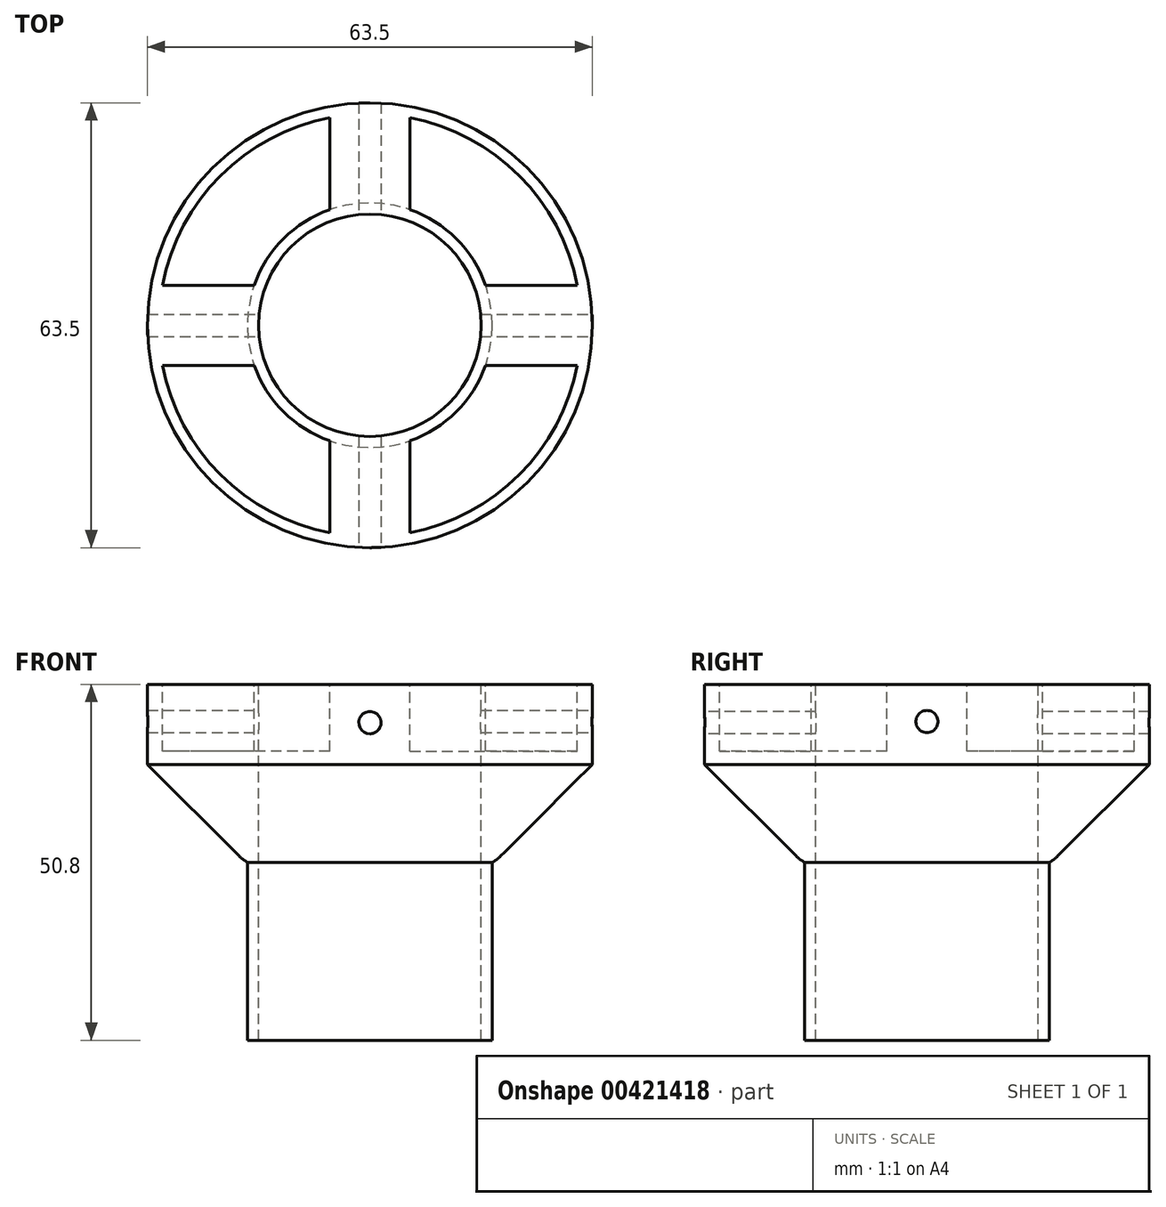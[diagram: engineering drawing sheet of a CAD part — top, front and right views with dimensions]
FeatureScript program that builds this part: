
annotation { "Feature Type Name" : "Feature", "Feature Type Description" : "" }
export const myFeature = defineFeature(function(context is Context, id is Id, definition is map)
    precondition{}
    {
        {
            var Q0;
            Q0=qCreatedBy(makeId("Top.planeOp"),FACE);
            var sketch = newSketch(context, id + "F0", { "sketchPlane" : qUnion([Q0])});
            skCircle(sketch, "E0", {"center": v(0, 0) * mm, "radius": 31.75 * mm});
            skCircle(sketch, "E1", {"center": v(0, 0) * mm, "radius": 15.88 * mm});
            skCircle(sketch, "E2", {"center": v(0, 0) * mm, "radius": 17.46 * mm});
            skSolve(sketch);
        }
        {
            var Q0;
            Q0 = qSketchRegion(id + "F0", true);
            extrude(context, id + "F1", {"entities" : qUnion([Q0]), "oppositeDirection" : true, "depth" : 25.4 * mm});
        }
        {
            var Q0;
            Q0=makeQuery(id+"F0.imprint","IMPRINT",FACE,{"disambiguationData":[TD([[makeQuery(id+"F0.imprint","IMPRINT",EDGE,{"derivedFrom":sQuery(id+"F0.wireOp",EDGE,"E1")}),-1.0]])]});
            extrude(context, id + "F2", {"entities" : qUnion([Q0]), "operationType" : NewBodyOperationType.ADD, "oppositeDirection" : true, "depth" : 50.8 * mm});
        }
        {
            var Q0;
            Q0=makeQuery(id+"F1.opExtrude","CAP_EDGE",EDGE,{"disambiguationData":[OSD([sQuery(id+"F0.wireOp",EDGE,"E0")])],"isStart":false});
            chamfer(context, id + "F3", {"entities" : qUnion([Q0]), "width" : 13.97 * mm, "tangentPropagation" : true});
        }
        {
            var Q0;
            {var subQ0=sQuery(id+"F0.wireOp",EDGE,"E0");Q0=makeQuery(id+"F3.opChamfer","BLEND_EDGE",EDGE,{"blendedFrom":[makeQuery(id+"F1.opExtrude","CAP_EDGE",EDGE,{"disambiguationData":[OSD([subQ0])],"isStart":false}),makeQuery(id+"F1.opExtrude","CAP_FACE",FACE,{"disambiguationData":[OSD([subQ0,sQuery(id+"F0.wireOp",EDGE,"E2")])],"isStart":false})],"blendedInto":[makeQuery(id+"F1.opExtrude","CAP_FACE",FACE,{"disambiguationData":[OSD([subQ0,sQuery(id+"F0.wireOp",EDGE,"E2")])],"isStart":false})]});}
            fillet(context, id + "F4", {"entities" : qUnion([Q0]), "radius" : 5.08 * mm, "tangentPropagation" : true, "allowEdgeOverflow" : false});
        }
        {
            var Q0;
            Q0=qCreatedBy(makeId("Top.planeOp"),FACE);
            var sketch = newSketch(context, id + "F5", { "sketchPlane" : qUnion([Q0])});
            skLineSegment(sketch, "E3.bottom", {"start": v(5.72, -31.75) * mm, "end": v(-5.71, -31.75) * mm});
            skLineSegment(sketch, "E3.top", {"start": v(5.71, 31.75) * mm, "end": v(-5.72, 31.75) * mm});
            skLineSegment(sketch, "E3.left", {"start": v(5.72, -31.75) * mm, "end": v(5.71, 31.75) * mm});
            skLineSegment(sketch, "E3.right", {"start": v(-5.72, -31.75) * mm, "end": v(-5.72, 31.75) * mm});
            skPoint(sketch, "E3.middle", {"position": v(0, 0) * mm});
            skLineSegment(sketch, "E4.bottom", {"start": v(31.75, -5.71) * mm, "end": v(-31.75, -5.72) * mm});
            skLineSegment(sketch, "E4.top", {"start": v(31.75, 5.72) * mm, "end": v(-31.75, 5.71) * mm});
            skLineSegment(sketch, "E4.left", {"start": v(31.75, -5.71) * mm, "end": v(31.75, 5.72) * mm});
            skLineSegment(sketch, "E4.right", {"start": v(-31.75, -5.72) * mm, "end": v(-31.75, 5.71) * mm});
            skCircle(sketch, "E5", {"center": v(0, 0) * mm, "radius": 30.16 * mm});
            skCircle(sketch, "E6", {"center": v(0, 0) * mm, "radius": 17.46 * mm});
            skSolve(sketch);
        }
        {
            var Q0;
            {var subQ0=sQuery(id+"F5.wireOp",EDGE,"E5");var subQ1=sQuery(id+"F5.wireOp",EDGE,"E3.right");var subQ2=makeQuery(id+"F5.imprint","INTERSECT",VERTEX,{"disambiguationData":[OD(1.0)],"derivedFrom":[subQ1,subQ0]});Q0=makeQuery(id+"F5.imprint","IMPRINT",FACE,{"disambiguationData":[TD([[makeQuery(id+"F5.imprint","IMPRINT",EDGE,{"disambiguationData":[TD([[subQ2,1.0]])],"derivedFrom":subQ1}),1.0]])]});}
            var Q1;
            {var subQ0=sQuery(id+"F5.wireOp",EDGE,"E5");var subQ1=sQuery(id+"F5.wireOp",EDGE,"E3.right");var subQ2=makeQuery(id+"F5.imprint","INTERSECT",VERTEX,{"disambiguationData":[OD(0.0)],"derivedFrom":[subQ1,subQ0]});Q1=makeQuery(id+"F5.imprint","IMPRINT",FACE,{"disambiguationData":[TD([[makeQuery(id+"F5.imprint","IMPRINT",EDGE,{"disambiguationData":[TD([[subQ2,-1.0]])],"derivedFrom":subQ1}),1.0]])]});}
            var Q2;
            {var subQ0=sQuery(id+"F5.wireOp",EDGE,"E5");var subQ1=sQuery(id+"F5.wireOp",EDGE,"E3.left");var subQ2=makeQuery(id+"F5.imprint","INTERSECT",VERTEX,{"disambiguationData":[OD(0.0)],"derivedFrom":[subQ1,subQ0]});Q2=makeQuery(id+"F5.imprint","IMPRINT",FACE,{"disambiguationData":[TD([[makeQuery(id+"F5.imprint","IMPRINT",EDGE,{"disambiguationData":[TD([[subQ2,-1.0]])],"derivedFrom":subQ1}),-1.0]])]});}
            var Q3;
            {var subQ0=sQuery(id+"F5.wireOp",EDGE,"E5");var subQ1=sQuery(id+"F5.wireOp",EDGE,"E3.left");var subQ2=makeQuery(id+"F5.imprint","INTERSECT",VERTEX,{"disambiguationData":[OD(1.0)],"derivedFrom":[subQ1,subQ0]});Q3=makeQuery(id+"F5.imprint","IMPRINT",FACE,{"disambiguationData":[TD([[makeQuery(id+"F5.imprint","IMPRINT",EDGE,{"disambiguationData":[TD([[subQ2,1.0]])],"derivedFrom":subQ1}),-1.0]])]});}
            extrude(context, id + "F6", {"entities" : qUnion([Q0, Q1, Q2, Q3]), "operationType" : NewBodyOperationType.REMOVE, "oppositeDirection" : true, "depth" : 9.52 * mm});
        }
        {
            var Q0;
            Q0=qCreatedBy(makeId("Top.planeOp"),FACE);
            cPlane(context, id + "F7", {"entities" : qUnion([Q0]), "cplaneType" : CPlaneType.OFFSET, "offset" : 5.46 * mm, "oppositeDirection" : true, "width" : 152.4 * mm, "height" : 152.4 * mm});
        }
        {
            var Q0;
            Q0=qCreatedBy(makeId("Front.planeOp"),FACE);
            cPlane(context, id + "F8", {"entities" : qUnion([Q0]), "cplaneType" : CPlaneType.OFFSET, "offset" : 50.8 * mm, "width" : 152.4 * mm, "height" : 152.4 * mm});
        }
        {
            var Q0;
            Q0=qCreatedBy(id+"F8.planeOp",FACE);
            var sketch = newSketch(context, id + "F9", { "sketchPlane" : qUnion([Q0])});
            skPoint(sketch, "E7", {"position": v(0, -5.47) * mm});
            skSolve(sketch);
        }
        {
            var Q0;
            Q0=sQuery(id+"F9.wireOp",VERTEX,"E7");
            var Q1;
            Q1=makeQuery(id+"F1.opExtrude","SWEPT_BODY",BODY,{"disambiguationData":[OSD([sQuery(id+"F0.wireOp",EDGE,"E0"),sQuery(id+"F0.wireOp",EDGE,"E2")])]});
            hole(context, id + "F10", {"style" : HoleStyle.SIMPLE, "endStyle" : HoleEndStyle.THROUGH, "holeDiameter" : 3.17 * mm, "isTappedThrough" : true, "tappedDepth" : 12.7 * mm, "tapClearance" : 3, "locations" : qUnion([Q0]), "scope" : qUnion([Q1])});
        }
        {
            var Q0;
            Q0=qCreatedBy(makeId("Right.planeOp"),FACE);
            cPlane(context, id + "F11", {"entities" : qUnion([Q0]), "cplaneType" : CPlaneType.OFFSET, "offset" : 50.8 * mm, "width" : 152.4 * mm, "height" : 152.4 * mm});
        }
        {
            var Q0;
            Q0=qCreatedBy(id+"F11.planeOp",FACE);
            var sketch = newSketch(context, id + "F12", { "sketchPlane" : qUnion([Q0])});
            skPoint(sketch, "E8", {"position": v(0, -5.32) * mm});
            skSolve(sketch);
        }
        {
            var Q0;
            Q0=sQuery(id+"F12.wireOp",VERTEX,"E8");
            var Q1;
            Q1=makeQuery(id+"F1.opExtrude","SWEPT_BODY",BODY,{"disambiguationData":[OSD([sQuery(id+"F0.wireOp",EDGE,"E0"),sQuery(id+"F0.wireOp",EDGE,"E2")])]});
            hole(context, id + "F13", {"style" : HoleStyle.SIMPLE, "endStyle" : HoleEndStyle.THROUGH, "holeDiameter" : 3.17 * mm, "isTappedThrough" : true, "tappedDepth" : 12.7 * mm, "tapClearance" : 3, "locations" : qUnion([Q0]), "scope" : qUnion([Q1])});
        }
    });
